# Revit family: LEGRAND_NON INTERLOCKED SOCKETS_FLUSH MOUNTED_IP44_400
name_source: partatom
category: Installations électriques
revit_build: Autodesk Revit 2018 (Build: 20170223_1515(x64)
units: mm (PartAtom-declared; Revit-internal decimal feet)

## family parameters
Conserver l'orientation des annotations = Non
Cote de connecteur circulaire = Utiliser le diamètre
Couper avec des vides une fois chargée = Non
Hôte = Face
Partagée = Non
Point de calcul de pièce = Non
Type d'élément = Normal

## types (19) — shared parameters
Description = international standard socket for flush or surface mounting with accessory allows the connection of power devices
Elévation par défaut = 1000 mm  [stored 3.28084 ft]
Fabricant = Legrand
Flush E or Surface mounting S = flush and surface mounting
General Conditions of Use = https://export.legrand.com
Maximum installation temperature = 40°C
Maximum use temperature = 100°C
Minimum installation temperature = -20°C
Minimum use temperature = -50°C
Standard IEC or NFC = IEC
Tension V = 400 V  50/60 Hz red
characteristic color = red
connecting type = screw terminals
halogen free = Oui
protection class IP = IP44

## per-type parameters (varying)
| type | Dia bouchon | Modèle | Number of poles | Position of earth h | RAY BOUCHON | Ray | depth for flush mounting mm | depth mm | h1 | height mm | horizontal fixing distance mm | intensity A | material of box | resistance to chocks IK | vertical fixing distance mm | width mm |
| panel mounting socket à single fixing center Hypra   IP44   16 A   380/415 V   2P+E   plast | 55 mm | 052218 | 3 | 9 | 27 mm | 27 mm | 37 mm | 73 mm  [stored 0.239501 ft] | 50 mm | 84 mm | 70 mm | 16 A | plastic | 09 | 70 mm | 84 mm |
| panel mounting socket à single fixing center Hypra   IP44   16 A   380/415 V   3P+E   plast | 55 mm | 052219 | 3 | 9 | 27 mm | 27 mm | 43 mm | 84 mm | 50 mm | 84 mm | 70 mm | 16 A | plastic | 09 | 70 mm | 84 mm |
| panel mounting socket à single fixing center Hypra   IP44   16 A   380/415 V   3P+N+E   plast | 55 mm | 052220 | 5 | 6 | 27 mm | 27 mm | 43 mm | 80 mm | 50 mm | 84 mm | 70 mm | 16 A | plastic | 09 | 70 mm | 84 mm |
| panel mounting socket Hypra   IP44   16 A   380/415 V   2P+E   plast | 42 mm | 052222 | 3 | 9 | 21 mm  [stored 0.0688976 ft] | 21 mm  [stored 0.0688976 ft] | 41 mm | 81 mm | 43 mm | 72 mm | 52 mm | 16 A | plastic | 09 | 60 mm | 64 mm |
| panel mounting socket Hypra   IP44   16 A   380/415 V   3P+E   plast | 48 mm | 052223 | 3 | 9 | 24 mm | 24 mm | 44 mm | 84 mm | 50 mm | 84 mm | 60 mm | 16 A | plastic | 09 | 70 mm | 74 mm |
| panel mounting socket Hypra   IP44   16 A   380/415 V   3P+N+E   plast | 48 mm | 052224 | 5 | 6 | 24 mm | 24 mm | 44 mm | 88 mm | 50 mm | 84 mm | 60 mm | 16 A | plastic | 09 | 70 mm | 74 mm |
| panel mounting socket Hypra   IP44   16 A   380/415 V   2P+E   métal | 42 mm | 052232 | 3 | 9 | 21 mm  [stored 0.0688976 ft] | 21 mm  [stored 0.0688976 ft] | 41 mm | 81 mm | 43 mm | 72 mm | 52 mm | 16 A | metal | 10 | 60 mm | 64 mm |
| panel mounting socket Hypra   IP44   16 A   380/415 V   3P+E   métal | 48 mm | 052233 | 4 | 6 | 24 mm | 24 mm | 44 mm | 84 mm | 50 mm | 84 mm | 60 mm | 16 A | metal | 10 | 70 mm | 74 mm |
| panel mounting socket Hypra   IP44   16 A   380/415 V   3P+N+E   métal | 48 mm | 052234 | 5 | 6 | 24 mm | 24 mm | 44 mm | 88 mm | 50 mm | 84 mm | 60 mm | 16 A | metal | 10 | 70 mm | 74 mm |
| panel mounting socket  Hypra   IP44   32 A   380/415 V   2P+E   plast | 55 mm | 052918 | 3 | 9 | 27 mm | 27 mm | 50 mm | 103 mm | 56 mm | 94 mm | 70 mm | 32 A | plastic | 09 | 70 mm | 84 mm |
| panel mounting socket Hypra   IP44   32 A   380/415 V   3P+E   plast | 55 mm | 052919 | 4 | 6 | 27 mm | 27 mm | 50 mm | 103 mm | 56 mm | 94 mm | 70 mm | 32 A | plastic | 09 | 70 mm | 84 mm |
| panel mounting socket Hypra   IP44   32 A   380/415 V   3P+N+E   plast | 55 mm | 052920 | 5 | 6 | 27 mm | 27 mm | 52 mm | 108 mm | 56 mm | 94 mm | 70 mm | 32 A | plastic | 09 | 70 mm | 84 mm |
| panel mounting socket Hypra   IP44   32 A   380/415 V   2P+E   métal | 55 mm | 052932 | 3 | 9 | 27 mm | 27 mm | 50 mm | 103 mm | 56 mm | 94 mm | 70 mm | 32 A | metal | 10 | 70 mm | 84 mm |
| panel mounting socket Hypra   IP44   32 A   380/415 V   3P+E   métal | 55 mm | 052934 | 4 | 6 | 27 mm | 27 mm | 50 mm | 103 mm | 56 mm | 94 mm | 70 mm | 32 A | metal | 10 | 70 mm | 84 mm |
| panel mounting socket Hypra   IP44   32 A   380/415 V   3P+N+E   métal | 55 mm | 052934 | 5 | 6 | 27 mm | 27 mm | 52 mm | 108 mm | 56 mm | 94 mm | 70 mm | 32 A | metal | 10 | 80 mm | 84 mm |
| panel mounting socket Hypra   IP44   63 A   380/415 V   3P+E   plast | 69 mm | 053823 | 4 | 6 | 34 mm | 34 mm | 98 mm | 168 mm | 64 mm | 106 mm | 77 mm | 63 A | plastic | 09 | 85 mm | 106 mm |
| panel mounting socket Hypra   IP44   63 A   380/415 V   3P+N+E   plast | 69 mm | 053824 | 4 | 6 | 34 mm | 34 mm | 98 mm | 168 mm | 64 mm | 106 mm | 77 mm | 63 A | plastic | 09 | 85 mm | 106 mm |
| panel mounting socket Hypra   IP44   63 A   380/415 V   3P+E   métal | 69 mm | 053833 | 4 | 6 | 34 mm | 34 mm | 98 mm | 168 mm | 64 mm | 106 mm | 77 mm | 63 A | metal | 10 | 85 mm | 106 mm |
| panel mounting socket Hypra   IP44   63 A   380/415 V   3P+N+E   métal | 69 mm | 053834 | 5 | 6 | 34 mm | 34 mm | 98 mm | 168 mm | 64 mm | 106 mm | 77 mm | 63 A | metal | 10 | 85 mm | 106 mm |

note: [stored X ft] marks values corroborated as IEEE doubles in the binary element streams (Revit-internal decimal feet)
